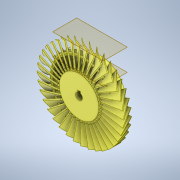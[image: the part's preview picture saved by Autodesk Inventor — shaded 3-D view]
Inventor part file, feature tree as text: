
AUTODESK INVENTOR PART (.ipt)
format: ipt  version: 2021.2 (Build 252289000, 289)  size: 4,991,488 bytes
history: native  units: in
note: dims shown in document units (in); Inventor stores cm internally (conversion verified against a paired STEP export)
features: sketch x6, extrude x5, plane x2, other x2, revolve x1, loft x1, pattern_circular x1
ambient origin geometry x8: Origin, YZ Plane, XZ Plane, XY Plane, X Axis, Y Axis, Z Axis, Center Point
bodies: Solid1 (feature_tree)
feature tree (18):
  extrude  "Extrusion1"  Depth=1.0in
  plane  "Work Plane1"
  sketch  "Sketch2"  dims[d3=1.0in d7=2.0in]
  plane  "Work Plane2"
  sketch  "Sketch3"  dims[d22=0.315in d23=0.125in]
  extrude  "Extrusion3"  Depth=2.0in
  sketch  "Sketch6"  dims[d27=3.9375in d36=0.5in]
  revolve  "Revolution2"  [1 undecoded]
  extrude  "Extrusion6"  TaperAngle=0.0deg  [1 undecoded]
  extrude  "Extrusion7"  Depth=0.5in
  loft  "Loft3"
  pattern_circular  "Circular Pattern3"  [2 undecoded]
  extrude  "Extrusion8"  Depth=0.5in
  sketch  "Sketch1"  dims[d0=1.8in d1=1.0in d2=0.0777in]
  sketch  "Sketch5"  dims[d24=0.125in d25=0.0in d26=0.0in]
  sketch  "Sketch7"  dims[d37=0.0312in d38=0.0625in d42=0.125in d43=0.5in d45=0.3in d46=0.0in d47=0.05in d48=90.0deg d51=1.6063in d52=1.3631in d54=0.0068in d57=0.0433in d58=0.0087in d62=0.0349in d63=0.1998in d64=0.0619in d65=0.0318in d66=0.0349in d67=0.2in d68=0.0in d69=0.023in d70=0.1in d71=0.0in d72=0.0in d73=90.0deg d74=0.0in d75=90.0deg d76=14.1732in d77=360.0deg d79=0.0in d80=0.0in]
  other  "Edges3"
  other  "Edges4"
note: 4 required parameter values undecoded (feature->parameter linkage not recoverable at this tier; creation-order binding heuristic only, values carry confidence <= 0.55)